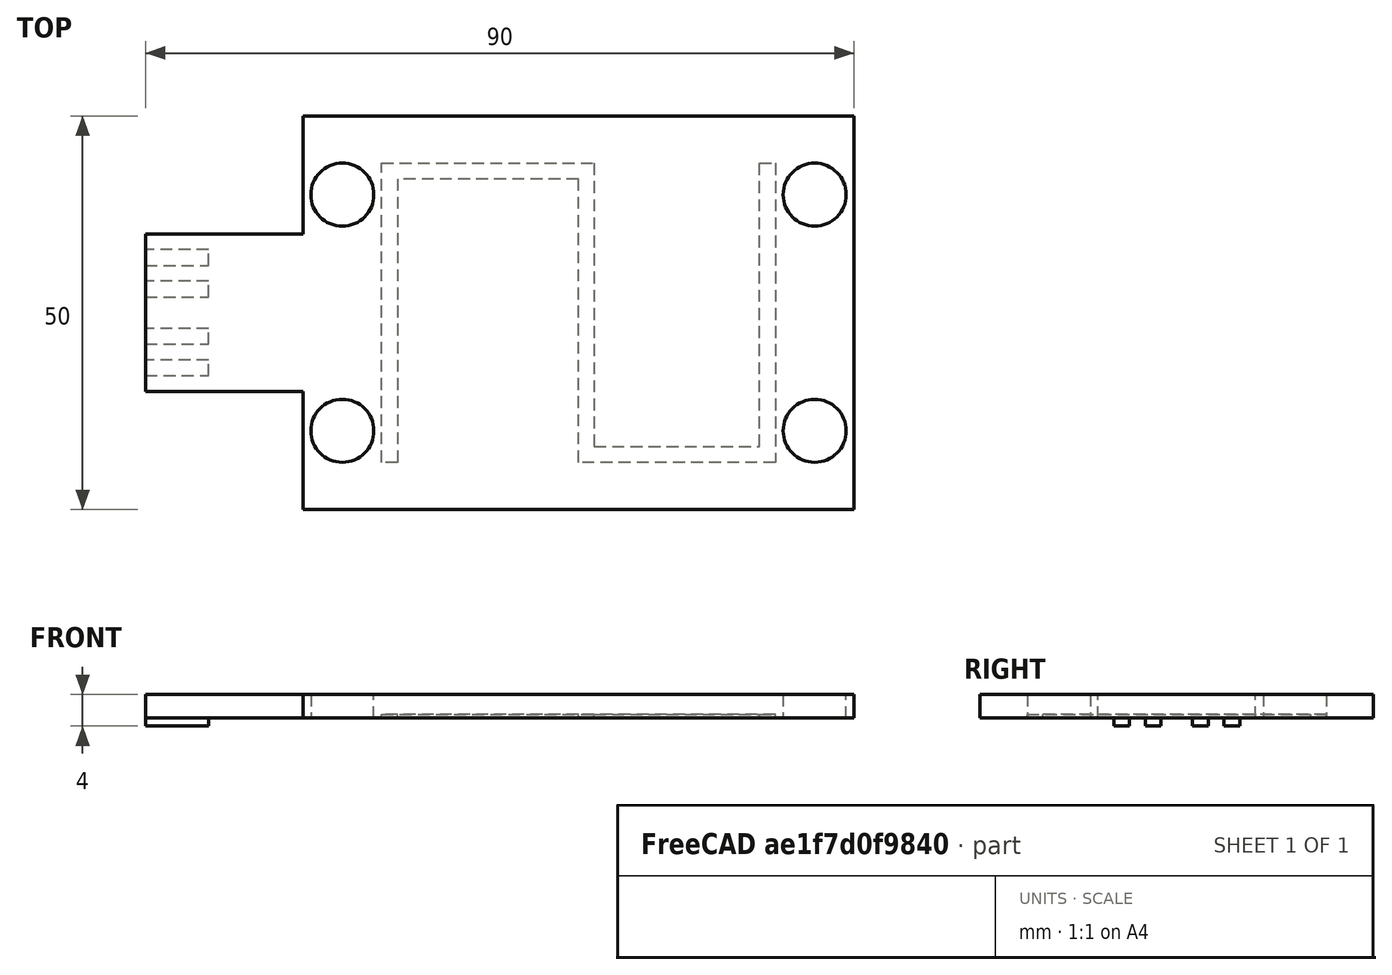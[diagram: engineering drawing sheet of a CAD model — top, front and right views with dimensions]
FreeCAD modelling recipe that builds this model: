
FCSTD DOCUMENT  (FreeCAD 0.16R6712 (Git))
Label: py_pcb
License: All rights reserved
LicenseURL: http://en.wikipedia.org/wiki/All_rights_reserved
objects: Sketcher::SketchObject×6, Part::Extrusion×2, PartDesign::Pocket×2
note: 12 computed .brp shape members not serialized (recipe doc carries the construction recipe); baked Part::Feature solids carry a one-line shape summary decoded from their .brp

FEATURE [Sketcher::SketchObject] Sketch
  sketch-geometry (8):
    g0: LineSegment StartX=0 StartY=10 StartZ=0 EndX=0 EndY=-10 EndZ=0
    g1: LineSegment StartX=0 StartY=10 StartZ=0 EndX=20 EndY=10 EndZ=0
    g2: LineSegment StartX=0 StartY=-10 StartZ=0 EndX=20 EndY=-10 EndZ=0
    g3: LineSegment StartX=20 StartY=10 StartZ=0 EndX=20 EndY=25 EndZ=0
    g4: LineSegment StartX=20 StartY=-10 StartZ=0 EndX=20 EndY=-25 EndZ=0
    g5: LineSegment StartX=20 StartY=25 StartZ=0 EndX=90 EndY=25 EndZ=0
    g6: LineSegment StartX=20 StartY=-25 StartZ=0 EndX=90 EndY=-25 EndZ=0
    g7: LineSegment StartX=90 StartY=25 StartZ=0 EndX=90 EndY=-25 EndZ=0
  constraints (9):
    c: PointOnObject(g0,g-2)
    c: PointOnObject(g0,g-2)
    c: Coincident(g1,g0)
    c: Coincident(g2,g0)
    c: Coincident(g3,g1)
    c: Coincident(g4,g2)
    c: Coincident(g5,g3)
    c: Coincident(g7,g5)
    c: Coincident(g7,g6)
FEATURE [Part::Extrusion] Extrude
  Base = -> Sketch
  Dir = (0,0,3)
  Solid = true
FEATURE [Sketcher::SketchObject] Sketch002
  Placement = pos=(0,0,0) rot=(1,0,0;3.14159rad)
  Support = -> Extrude [Face9]
  sketch-geometry (4):
    g0: Circle CenterX=25 CenterY=15 CenterZ=0 NormalX=0 NormalY=0 NormalZ=1 Radius=4
    g1: Circle CenterX=25 CenterY=-15 CenterZ=0 NormalX=0 NormalY=0 NormalZ=1 Radius=4
    g2: Circle CenterX=85 CenterY=-15 CenterZ=0 NormalX=0 NormalY=0 NormalZ=1 Radius=4
    g3: Circle CenterX=85 CenterY=15 CenterZ=0 NormalX=0 NormalY=0 NormalZ=1 Radius=4
FEATURE [PartDesign::Pocket] Pocket
  Length = 3
  Sketch = -> Sketch002
  Type = 0
FEATURE [Sketcher::SketchObject] Sketch003
  Placement = pos=(0,0,0) rot=(1,0,0;3.14159rad)
  Support = -> Pocket [Face4]
  sketch-geometry (16):
    g0: LineSegment StartX=0 StartY=8 StartZ=0 EndX=8 EndY=8 EndZ=0
    g1: LineSegment StartX=8 StartY=8 StartZ=0 EndX=8 EndY=6 EndZ=0
    g2: LineSegment StartX=8 StartY=6 StartZ=0 EndX=0 EndY=6 EndZ=0
    g3: LineSegment StartX=0 StartY=6 StartZ=0 EndX=0 EndY=8 EndZ=0
    g4: LineSegment StartX=0 StartY=4 StartZ=0 EndX=8 EndY=4 EndZ=0
    g5: LineSegment StartX=8 StartY=4 StartZ=0 EndX=8 EndY=2 EndZ=0
    g6: LineSegment StartX=8 StartY=2 StartZ=0 EndX=0 EndY=2 EndZ=0
    g7: LineSegment StartX=0 StartY=2 StartZ=0 EndX=0 EndY=4 EndZ=0
    g8: LineSegment StartX=0 StartY=-2 StartZ=0 EndX=8 EndY=-2 EndZ=0
    g9: LineSegment StartX=8 StartY=-2 StartZ=0 EndX=8 EndY=-4 EndZ=0
    g10: LineSegment StartX=8 StartY=-4 StartZ=0 EndX=0 EndY=-4 EndZ=0
    g11: LineSegment StartX=0 StartY=-4 StartZ=0 EndX=0 EndY=-2 EndZ=0
    g12: LineSegment StartX=0 StartY=-6 StartZ=0 EndX=8 EndY=-6 EndZ=0
    g13: LineSegment StartX=8 StartY=-6 StartZ=0 EndX=8 EndY=-8 EndZ=0
    g14: LineSegment StartX=8 StartY=-8 StartZ=0 EndX=0 EndY=-8 EndZ=0
    g15: LineSegment StartX=0 StartY=-8 StartZ=0 EndX=0 EndY=-6 EndZ=0
FEATURE [Part::Extrusion] Extrude001
  Base = -> Sketch003
  Dir = (0,0,-1)
  Solid = true
FEATURE [Sketcher::SketchObject] Sketch004
  Placement = pos=(0,0,0) rot=(1,0,0;3.14159rad)
  Support = -> Pocket [Face4]
  sketch-geometry (12):
    g0: LineSegment StartX=30 StartY=19 StartZ=0 EndX=30 EndY=-19 EndZ=0
    g1: LineSegment StartX=30 StartY=-19 StartZ=0 EndX=57 EndY=-19 EndZ=0
    g2: LineSegment StartX=57 StartY=-19 StartZ=0 EndX=57 EndY=17 EndZ=0
    g3: LineSegment StartX=57 StartY=17 StartZ=0 EndX=78 EndY=17 EndZ=0
    g4: LineSegment StartX=78 StartY=17 StartZ=0 EndX=78 EndY=-19 EndZ=0
    g5: LineSegment StartX=78 StartY=-19 StartZ=0 EndX=80 EndY=-19 EndZ=0
    g6: LineSegment StartX=80 StartY=-19 StartZ=0 EndX=80 EndY=19 EndZ=0
    g7: LineSegment StartX=80 StartY=19 StartZ=0 EndX=55 EndY=19 EndZ=0
    g8: LineSegment StartX=55 StartY=19 StartZ=0 EndX=55 EndY=-17 EndZ=0
    g9: LineSegment StartX=55 StartY=-17 StartZ=0 EndX=32 EndY=-17 EndZ=0
    g10: LineSegment StartX=32 StartY=-17 StartZ=0 EndX=32 EndY=19 EndZ=0
    g11: LineSegment StartX=32 StartY=19 StartZ=0 EndX=30 EndY=19 EndZ=0
FEATURE [PartDesign::Pocket] Pocket001
  Length = 0.5
  Sketch = -> Sketch004
  Type = 0
FEATURE [Sketcher::SketchObject] Sketch005
  Placement = pos=(0,0,0) rot=(1,0,0;3.14159rad)
  Support = -> Pocket001 [Face4]
  sketch-geometry (4):
    g0: LineSegment StartX=20 StartY=25 StartZ=0 EndX=90 EndY=25 EndZ=0
    g1: LineSegment StartX=90 StartY=25 StartZ=0 EndX=90 EndY=-25 EndZ=0
    g2: LineSegment StartX=90 StartY=-25 StartZ=0 EndX=20 EndY=-25 EndZ=0
    g3: LineSegment StartX=20 StartY=-25 StartZ=0 EndX=20 EndY=25 EndZ=0
FEATURE [Sketcher::SketchObject] Sketch006
  Placement = pos=(0,0,0) rot=(1,0,0;3.14159rad)
  Support = -> Pocket [Face4]
